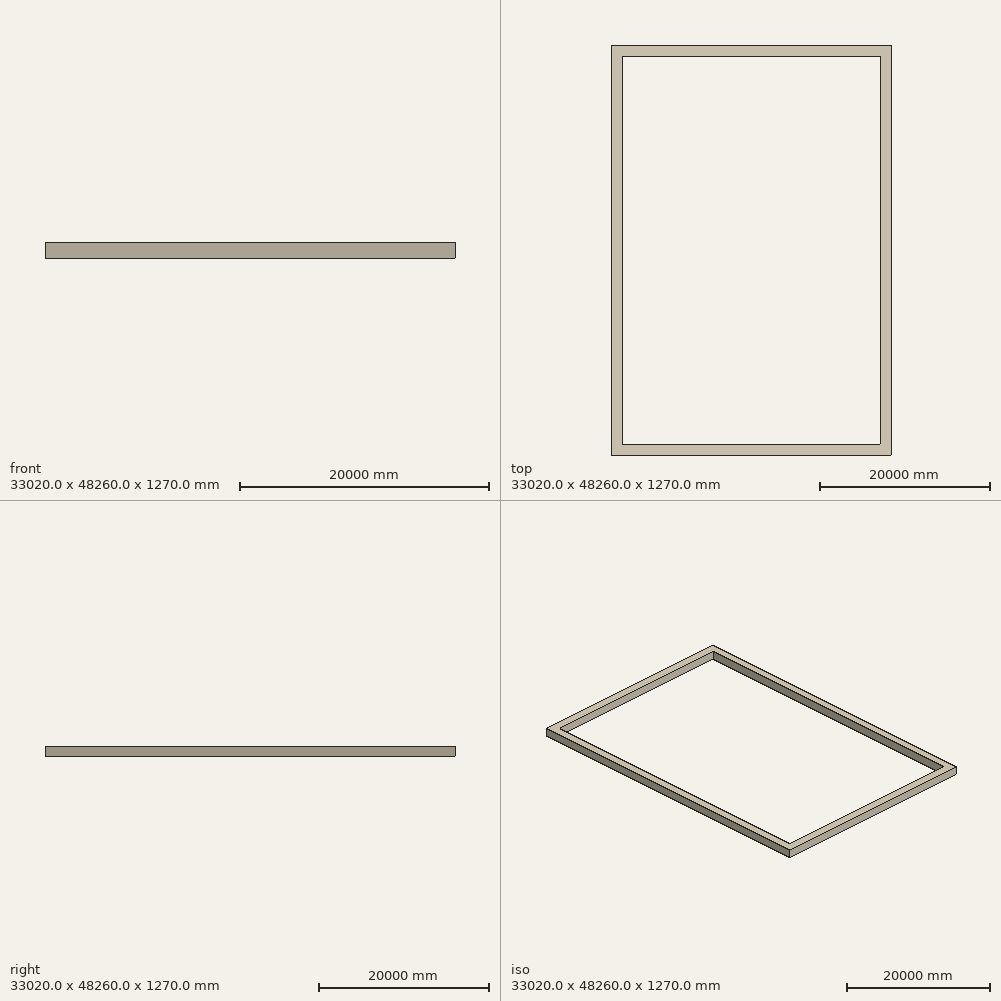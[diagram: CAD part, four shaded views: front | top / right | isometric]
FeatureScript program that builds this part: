
annotation { "Feature Type Name" : "Feature", "Feature Type Description" : "" }
export const myFeature = defineFeature(function(context is Context, id is Id, definition is map)
    precondition{}
    {
        {
            var Q0;
            Q0=qCreatedBy(makeId("Top.planeOp"),FACE);
            var sketch = newSketch(context, id + "F0", { "sketchPlane" : qUnion([Q0])});
            skLineSegment(sketch, "E0.bottom", {"start": v(-15240, -22860) * mm, "end": v(15240, -22860) * mm});
            skLineSegment(sketch, "E0.top", {"start": v(-15240, 22860) * mm, "end": v(15240, 22860) * mm});
            skLineSegment(sketch, "E0.left", {"start": v(-15240, -22860) * mm, "end": v(-15240, 22860) * mm});
            skLineSegment(sketch, "E0.right", {"start": v(15240, -22860) * mm, "end": v(15240, 22860) * mm});
            skLineSegment(sketch, "E1", {"start": v(0, 22583.68) * mm, "end": v(0, -10289.24) * mm, "construction": true});
            skLineSegment(sketch, "E2", {"start": v(0, 0) * mm, "end": v(-20302.35, 0) * mm, "construction": true});
            skLineSegment(sketch, "E3.0", {"start": v(-16510, -24130) * mm, "end": v(-16510, 24130) * mm});
            skLineSegment(sketch, "E3.1", {"start": v(-16510, -24130) * mm, "end": v(16510, -24130) * mm});
            skLineSegment(sketch, "E3.2", {"start": v(16510, -24130) * mm, "end": v(16510, 24130) * mm});
            skLineSegment(sketch, "E3.3", {"start": v(-16510, 24130) * mm, "end": v(16510, 24130) * mm});
            skSolve(sketch);
        }
        {
            var Q0;
            Q0 = qSketchRegion(id + "F0", true);
            extrude(context, id + "F1", {"entities" : qUnion([Q0]), "depth" : 1270 * mm, "offsetDistance" : 25.4 * mm});
        }
    });
